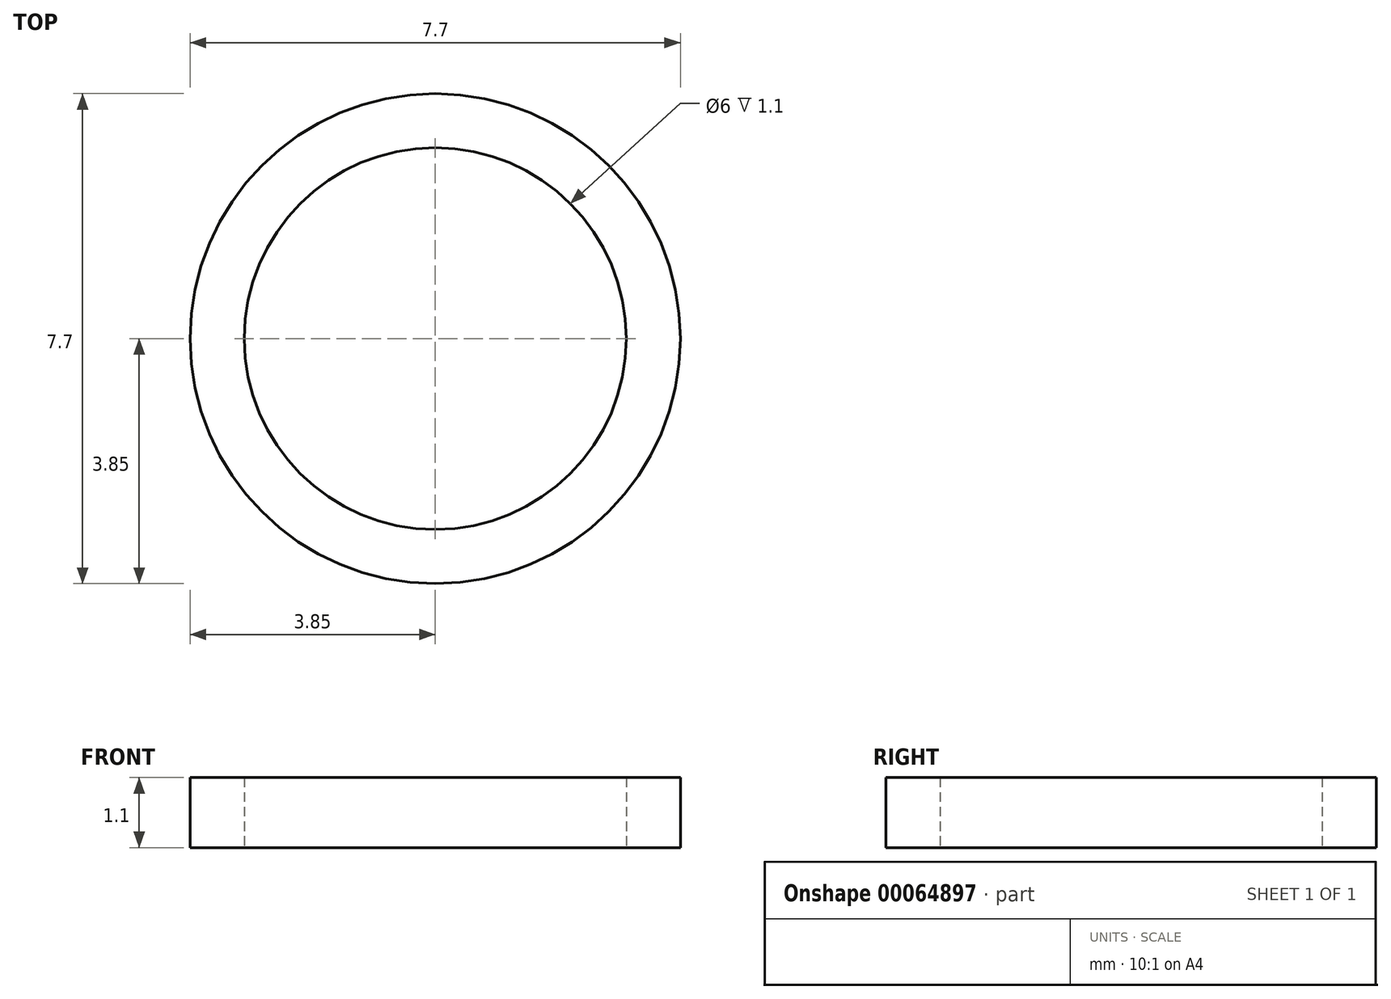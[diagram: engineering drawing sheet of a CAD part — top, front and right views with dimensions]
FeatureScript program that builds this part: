
annotation { "Feature Type Name" : "Feature", "Feature Type Description" : "" }
export const myFeature = defineFeature(function(context is Context, id is Id, definition is map)
    precondition{}
    {
        {
            var Q0;
            Q0=qCreatedBy(makeId("Top.planeOp"),FACE);
            var sketch = newSketch(context, id + "F0", { "sketchPlane" : qUnion([Q0])});
            skCircle(sketch, "E0", {"center": v(0, 0) * mm, "radius": 3 * mm});
            skCircle(sketch, "E1", {"center": v(0, 0) * mm, "radius": 3.85 * mm});
            skSolve(sketch);
        }
        {
            var Q0;
            Q0=makeQuery(id+"F0.imprint","IMPRINT",FACE,{"disambiguationData":[TD([[makeQuery(id+"F0.imprint","IMPRINT",EDGE,{"derivedFrom":sQuery(id+"F0.wireOp",EDGE,"E0")}),-1.0]])]});
            extrude(context, id + "F1", {"entities" : qUnion([Q0]), "depth" : 1.1 * mm});
        }
    });
